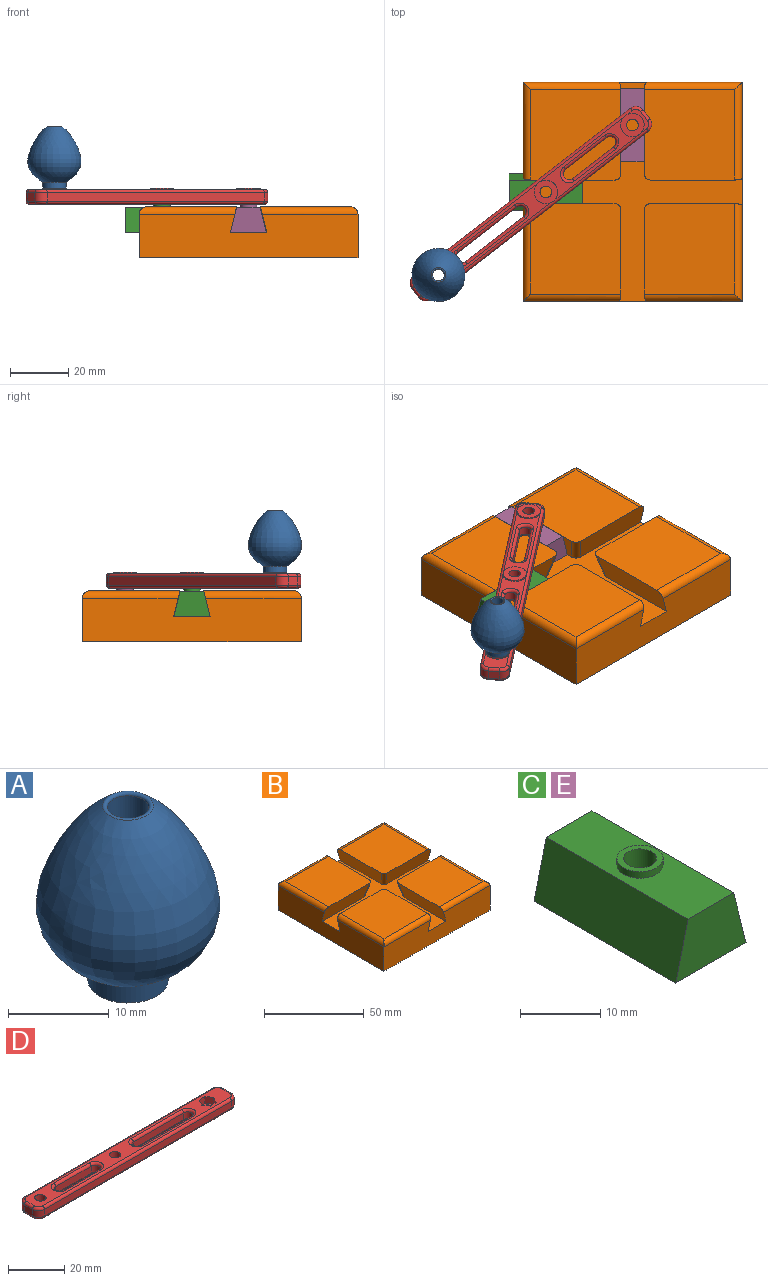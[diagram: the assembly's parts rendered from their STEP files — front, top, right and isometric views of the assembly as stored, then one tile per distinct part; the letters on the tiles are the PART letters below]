
ASSEMBLY  parts=5 mates=5
PART A: 5 faces, bbox 18.3x18.3x21.3 mm
  f0: cylinder r=4mm len=8mm, axis (0,0,-1), area 50.3mm2, adj f1,f2
  f1: revolved ~19.21x18.3mm, area 1009.9mm2, adj f0,f4
  f2: plane 8x8mm, normal (0,0,-1), area 37.1mm2, adj f0,f3
  f3: cylinder r=2.05mm len=20.96mm, axis (0,0,-1), area 269.9mm2, adj f2,f4
  f4: torus R=2.35mm, axis (0,0,-1), area 9.1mm2, adj f1,f3
PART B: 30 faces, bbox 75x75x17.7 mm
  f0: plane 30.93x30.93mm, normal (0,0,1), area 956mm2, adj f2,f16,f22,f23,f26
  f1: plane 30.93x30.93mm, normal (0,0,1), area 956mm2, adj f3,f15,f24,f25,f28
  f2: plane 31.49x8.75mm, normal (-0.97,0,-0.24), area 272.8mm2, adj f0,f6,f11,f23,f26
  f3: plane 31.49x8.75mm, normal (0.97,0,-0.24), area 272.8mm2, adj f1,f6,f11,f24,f28
  f4: plane 30.93x30.93mm, normal (0,0,1), area 956mm2, adj f12,f17,f20,f21,f27
  f5: plane 75x15mm, normal (0,-1,0), area 1056.6mm2, adj f7,f8,f10,f11,f12,f13,f18,f20
  f6: plane 75x15mm, normal (0,1,0), area 1056.6mm2, adj f2,f3,f7,f8,f10,f11,f23,f24
  f7: plane 75x15mm, normal (-1,0,0), area 1056.6mm2, adj f5,f6,f10,f11,f14,f15,f19,f25
  f8: plane 75x15mm, normal (1,0,0), area 1056.6mm2, adj f5,f6,f10,f11,f16,f17,f21,f22
  f9: plane 30.93x30.93mm, normal (0,0,1), area 956mm2, adj f13,f14,f18,f19,f29
  f10: plane 75x75mm, normal (0,0,-1), area 5625mm2, adj f5,f6,f7,f8
  f11: plane 75x75mm, normal (0,0,1), area 1721.9mm2, adj f2,f3,f5,f6,f7,f8,f12,f13
  f12: plane 31.49x8.75mm, normal (-0.97,0,-0.24), area 272.8mm2, adj f4,f5,f11,f20,f27
  f13: plane 31.49x8.75mm, normal (0.97,0,-0.24), area 272.8mm2, adj f5,f9,f11,f18,f29
  f14: plane 31.49x8.75mm, normal (0,0.97,-0.24), area 272.8mm2, adj f7,f9,f11,f19,f29
  f15: plane 31.49x8.75mm, normal (0,-0.97,-0.24), area 272.8mm2, adj f1,f7,f11,f25,f28
  f16: plane 31.49x8.75mm, normal (0,-0.97,-0.24), area 272.8mm2, adj f0,f8,f11,f22,f26
  f17: plane 31.49x8.75mm, normal (0,0.97,-0.24), area 272.8mm2, adj f4,f8,f11,f21,f27
  f18: cylinder r=2.5mm len=33.43mm, axis (-1,0,0), area 126.8mm2, adj f5,f9,f13,f19
  f19: cylinder r=2.5mm len=33.43mm, axis (0,1,0), area 126.8mm2, adj f7,f9,f14,f18
  f20: cylinder r=2.5mm len=33.43mm, axis (-1,0,0), area 126.8mm2, adj f4,f5,f12,f21
  f21: cylinder r=2.5mm len=33.43mm, axis (0,-1,0), area 126.8mm2, adj f4,f8,f17,f20
  f22: cylinder r=2.5mm len=33.43mm, axis (0,-1,0), area 126.8mm2, adj f0,f8,f16,f23
  f23: cylinder r=2.5mm len=33.43mm, axis (1,0,0), area 126.8mm2, adj f0,f2,f6,f22
  f24: cylinder r=2.5mm len=33.43mm, axis (1,0,0), area 126.8mm2, adj f1,f3,f6,f25
  f25: cylinder r=2.5mm len=33.43mm, axis (0,1,0), area 126.8mm2, adj f1,f7,f15,f24
  f26: cylinder r=2mm len=9.11mm, axis (-0.24,-0.24,0.94), area 28.1mm2, adj f0,f2,f11,f16
  f27: cylinder r=2mm len=9.11mm, axis (0.24,-0.24,-0.94), area 28.1mm2, adj f4,f11,f12,f17
  f28: cylinder r=2mm len=9.11mm, axis (-0.24,0.24,-0.94), area 28.1mm2, adj f1,f3,f11,f15
  f29: cylinder r=2mm len=9.11mm, axis (0.24,0.24,0.94), area 28.1mm2, adj f9,f11,f13,f14
PART C: 16 faces, bbox 12.4x25x9.7 mm
  f0: plane 25x8.7mm, normal (-0.97,0,0.24), area 224.2mm2, adj f1,f3,f4,f5
  f1: plane 25x12.4mm, normal (0,0,-1), area 284.7mm2, adj f0,f2,f4,f5,f6,f7,f8,f9
  f2: plane 25x8.7mm, normal (0.97,0,0.24), area 224.2mm2, adj f1,f3,f4,f5
  f3: plane 25x8.06mm, normal (0,0,1), area 175.6mm2, adj f0,f2,f4,f5,f14
  f4: plane 12.4x8.7mm, normal (0,1,0), area 89mm2, adj f0,f1,f2,f3
  f5: plane 12.4x8.7mm, normal (0,-1,0), area 89mm2, adj f0,f1,f2,f3
  f6: plane 3.5x3.06mm, normal (0.19,-0.98,0), area 10.9mm2, adj f1,f7,f11,f12
  f7: plane 3.5x2.36mm, normal (-0.76,-0.65,0), area 10.9mm2, adj f1,f6,f8,f12
  f8: plane 3.5x2.95mm, normal (-0.94,0.33,0), area 10.9mm2, adj f1,f7,f9,f12
  f9: plane 3.5x3.06mm, normal (-0.19,0.98,0), area 10.9mm2, adj f1,f8,f10,f12
  f10: plane 3.5x2.36mm, normal (0.76,0.65,0), area 10.9mm2, adj f1,f9,f11,f12
  f11: plane 3.5x2.95mm, normal (0.94,-0.33,0), area 10.9mm2, adj f1,f6,f10,f12
  f12: plane 6.12x5.89mm, normal (0,0,-1), area 12.1mm2, adj f6,f7,f8,f9,f10,f11,f13
  f13: cylinder r=2.05mm len=6.2mm, axis (0,0,1), area 79.9mm2, adj f12,f15
  f14: cylinder r=2.88mm len=5.75mm, axis (0,0,-1), area 18.1mm2, adj f3,f15
  f15: plane 5.75x5.75mm, normal (0,0,1), area 12.8mm2, adj f13,f14
PART D: 69 faces, bbox 100.5x10.5x5.5 mm
  f0: cylinder r=2mm len=4mm, axis (0,0,-1), area 31.4mm2, adj f61,f68
  f1: plane 9x8mm, normal (0,0,-1), area 45.2mm2, adj f48,f50,f52,f54,f55,f60
  f2: plane 46.5x8mm, normal (0,0,-1), area 141.8mm2, adj f28,f29,f30,f31,f48,f55,f58,f60
  f3: plane 37.5x8mm, normal (0,0,-1), area 114.9mm2, adj f24,f25,f26,f27,f48,f55,f56,f58
  f4: plane 8x5mm, normal (0,0,-1), area 13.2mm2, adj f48,f49,f51,f53,f55,f56
  f5: plane 4x3mm, normal (-1,0,0), area 12mm2, adj f12,f15,f43,f51
  f6: plane 94x3mm, normal (0,-1,0), area 282mm2, adj f12,f13,f40,f48
  f7: plane 4x3mm, normal (1,0,0), area 12mm2, adj f13,f14,f44,f52
  f8: plane 94x3mm, normal (0,1,0), area 282mm2, adj f14,f15,f47,f55
  f9: plane 98x8mm, normal (0,0,1), area 415.4mm2, adj f10,f11,f32,f33,f34,f35,f36,f37
  f10: cylinder r=2mm len=5.5mm, axis (0,0,-1), area 69.1mm2, adj f9,f57
  f11: cylinder r=2mm len=5.5mm, axis (0,0,-1), area 69.1mm2, adj f9,f59
  f12: cylinder r=3mm len=3mm, axis (0,0,1), area 14.1mm2, adj f5,f6,f41,f49
  f13: cylinder r=3mm len=3mm, axis (0,0,-1), area 14.1mm2, adj f6,f7,f42,f50
  f14: cylinder r=3mm len=3mm, axis (0,0,1), area 14.1mm2, adj f7,f8,f46,f54
  f15: cylinder r=3mm len=3mm, axis (0,0,-1), area 14.1mm2, adj f5,f8,f45,f53
  f16: plane 25.28x3mm, normal (0,-1,0), area 75.8mm2, adj f17,f19,f31,f32
  f17: cylinder r=2mm len=4mm, axis (0,0,1), area 18.8mm2, adj f16,f18,f29,f33
  f18: plane 25.28x3mm, normal (0,1,0), area 75.8mm2, adj f17,f19,f28,f35
  f19: cylinder r=2mm len=4mm, axis (0,0,1), area 18.8mm2, adj f16,f18,f30,f34
  f20: plane 17.76x3mm, normal (0,-1,0), area 53.3mm2, adj f21,f23,f27,f36
  f21: cylinder r=2mm len=4mm, axis (0,0,1), area 18.8mm2, adj f20,f22,f25,f37
  f22: plane 17.76x3mm, normal (0,1,0), area 53.3mm2, adj f21,f23,f24,f39
  f23: cylinder r=2mm len=4mm, axis (0,0,1), area 18.8mm2, adj f20,f22,f26,f38
  f24: cylinder r=1mm len=17.76mm, axis (1,0,0), area 27.9mm2, adj f3,f22,f25,f26
  f25: torus R=3mm, axis (0,0,1), area 11.7mm2, adj f3,f21,f24,f27
  f26: torus R=3mm, axis (0,0,1), area 11.7mm2, adj f3,f23,f24,f27
  f27: cylinder r=1mm len=17.76mm, axis (-1,0,0), area 27.9mm2, adj f3,f20,f25,f26
  f28: cylinder r=1mm len=25.28mm, axis (1,0,0), area 39.7mm2, adj f2,f18,f29,f30
  f29: torus R=3mm, axis (0,0,1), area 11.7mm2, adj f2,f17,f28,f31
  f30: torus R=3mm, axis (0,0,1), area 11.7mm2, adj f2,f19,f28,f31
  f31: cylinder r=1mm len=25.28mm, axis (-1,0,0), area 39.7mm2, adj f2,f16,f29,f30
  f32: cylinder r=1mm len=25.28mm, axis (1,0,0), area 39.7mm2, adj f9,f16,f33,f34
  f33: torus R=3mm, axis (0,0,1), area 11.7mm2, adj f9,f17,f32,f35
  f34: torus R=3mm, axis (0,0,1), area 11.7mm2, adj f9,f19,f32,f35
  f35: cylinder r=1mm len=25.28mm, axis (-1,0,0), area 39.7mm2, adj f9,f18,f33,f34
  f36: cylinder r=1mm len=17.76mm, axis (1,0,0), area 27.9mm2, adj f9,f20,f37,f38
  f37: torus R=3mm, axis (0,0,1), area 11.7mm2, adj f9,f21,f36,f39
  f38: torus R=3mm, axis (0,0,1), area 11.7mm2, adj f9,f23,f36,f39
  f39: cylinder r=1mm len=17.76mm, axis (-1,0,0), area 27.9mm2, adj f9,f22,f37,f38
  f40: cylinder r=1mm len=94mm, axis (-1,0,0), area 147.7mm2, adj f6,f9,f41,f42
  f41: torus R=2mm, axis (0,0,1), area 6.5mm2, adj f9,f12,f40,f43
  f42: torus R=2mm, axis (0,0,1), area 6.5mm2, adj f9,f13,f40,f44
  f43: cylinder r=1mm len=4mm, axis (0,1,0), area 6.3mm2, adj f5,f9,f41,f45
  f44: cylinder r=1mm len=4mm, axis (0,-1,0), area 6.3mm2, adj f7,f9,f42,f46
  f45: torus R=2mm, axis (0,0,1), area 6.5mm2, adj f9,f15,f43,f47
  f46: torus R=2mm, axis (0,0,1), area 6.5mm2, adj f9,f14,f44,f47
  f47: cylinder r=1mm len=94mm, axis (1,0,0), area 147.7mm2, adj f8,f9,f45,f46
  f48: cylinder r=1mm len=94mm, axis (1,0,0), area 147.7mm2, adj f1,f2,f3,f4,f6,f49,f50
  f49: torus R=2mm, axis (0,0,1), area 6.5mm2, adj f4,f12,f48,f51
  f50: torus R=2mm, axis (0,0,1), area 6.5mm2, adj f1,f13,f48,f52
  f51: cylinder r=1mm len=4mm, axis (0,-1,0), area 6.3mm2, adj f4,f5,f49,f53
  f52: cylinder r=1mm len=4mm, axis (0,1,0), area 6.3mm2, adj f1,f7,f50,f54
  f53: torus R=2mm, axis (0,0,1), area 6.5mm2, adj f4,f15,f51,f55
  f54: torus R=2mm, axis (0,0,1), area 6.5mm2, adj f1,f14,f52,f55
  f55: cylinder r=1mm len=94mm, axis (-1,0,0), area 147.7mm2, adj f1,f2,f3,f4,f8,f53,f54
  f56: cylinder r=4mm len=8mm, axis (0,0,1), area 12.6mm2, adj f3,f4,f57
  f57: plane 8x8mm, normal (0,0,-1), area 37.7mm2, adj f10,f56
  f58: cylinder r=4mm len=8mm, axis (0,0,1), area 12.6mm2, adj f2,f3,f59
  f59: plane 8x8mm, normal (0,0,-1), area 37.7mm2, adj f11,f58
  f60: cylinder r=4mm len=8mm, axis (0,0,1), area 12.6mm2, adj f1,f2,f61
  f61: plane 8x8mm, normal (0,0,-1), area 37.7mm2, adj f0,f60
  f62: plane 3x2.78mm, normal (-0.89,0.45,0), area 9.4mm2, adj f9,f63,f67,f68
  f63: plane 3x2.61mm, normal (-0.84,-0.55,0), area 9.4mm2, adj f9,f62,f64,f68
  f64: plane 3.11x3mm, normal (0.06,-1,0), area 9.4mm2, adj f9,f63,f65,f68
  f65: plane 3x2.78mm, normal (0.89,-0.45,0), area 9.4mm2, adj f9,f64,f66,f68
  f66: plane 3x2.61mm, normal (0.84,0.55,0), area 9.4mm2, adj f9,f65,f67,f68
  f67: plane 3.11x3mm, normal (-0.06,1,0), area 9.4mm2, adj f9,f62,f66,f68
  f68: plane 6.23x5.57mm, normal (0,0,1), area 12.7mm2, adj f0,f62,f63,f64,f65,f66,f67
PART E: same geometry as C
PLACE A rot(axis=(0,0,1),37.7deg) t=(-66.5,-28.5,15.2)mm
PLACE B at identity fixed
PLACE C rot(axis=(0,0,1),90deg) t=(-17.21,-0.05,0)mm
PLACE D rot(axis=(-0.32,0.95,0),180deg) t=(7.76,22.61,14.7)mm
PLACE E rot(axis=(0.08,0.63,0.77),0deg) t=(-0.05,10.39,0)mm
MATE revolute D.f11 <-> C.f14  axis (0,0,-1) through (-29.71,-0.05,9.7)mm
MATE slider E.f4 <-> B.f5  axis (0,-1,0) through (-6.25,35.39,0)mm
MATE cylindrical E.f14 <-> D.f10  axis (0,0,1) through (-0.05,22.89,9.7)mm
MATE slider B.f7 <-> C.f4  axis (-1,0,0) through (-37.5,-6.25,0)mm
MATE fastened A.f0 <-> D.f0  axis (0,0,-1) through (-66.5,-28.5,15.2)mm
